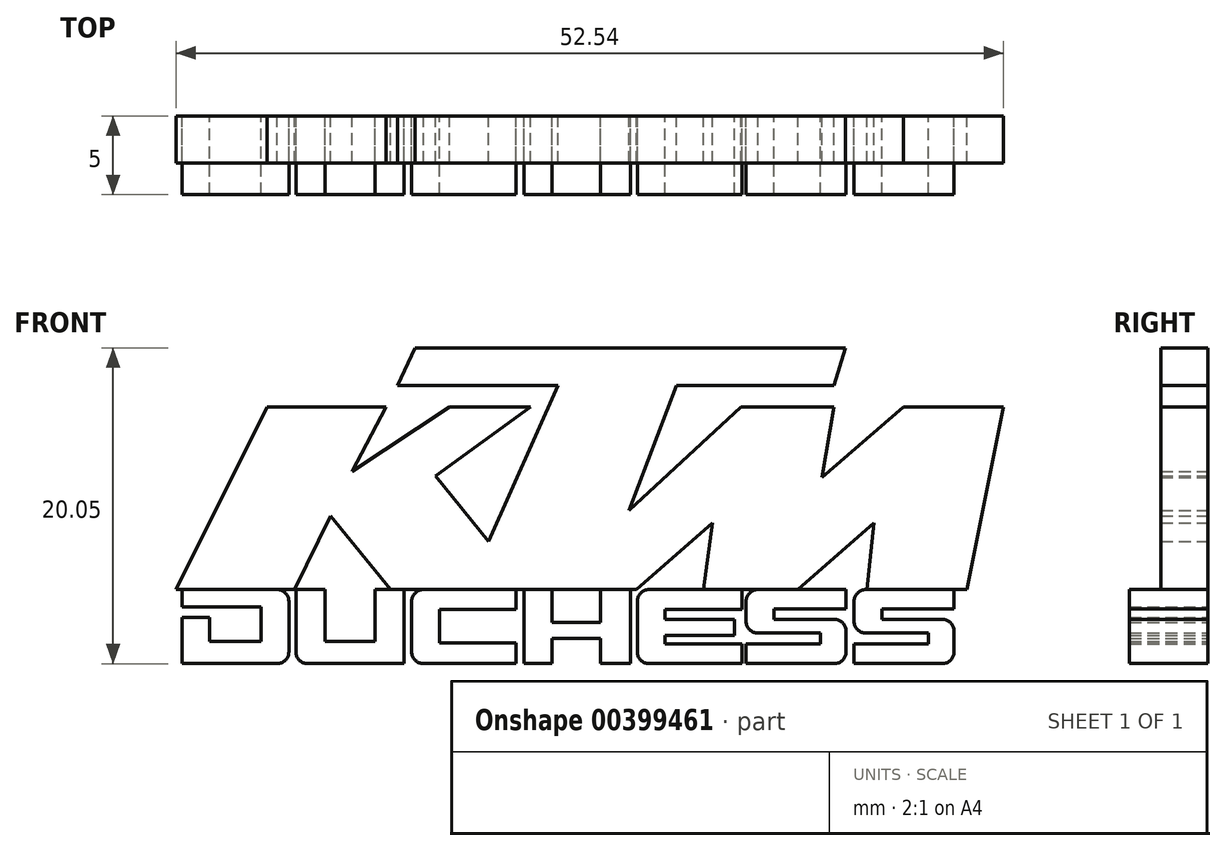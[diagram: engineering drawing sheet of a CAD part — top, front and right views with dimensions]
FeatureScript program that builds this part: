
annotation { "Feature Type Name" : "Feature", "Feature Type Description" : "" }
export const myFeature = defineFeature(function(context is Context, id is Id, definition is map)
    precondition{}
    {
        {
            var Q0;
            Q0=qCreatedBy(makeId("Front.planeOp"),FACE);
            var sketch = newSketch(context, id + "F0", { "sketchPlane" : qUnion([Q0])});
            skLineSegment(sketch, "E0", {"start": v(-21, 3.08) * mm, "end": v(-26.77, -8.53) * mm});
            skLineSegment(sketch, "E1", {"start": v(-19.24, -8.53) * mm, "end": v(-16.95, -3.85) * mm});
            skLineSegment(sketch, "E2", {"start": v(-16.95, -3.85) * mm, "end": v(-13.14, -8.53) * mm});
            skLineSegment(sketch, "E3", {"start": v(2.46, -8.53) * mm, "end": v(7.3, -4.3) * mm});
            skLineSegment(sketch, "E4", {"start": v(7.3, -4.3) * mm, "end": v(6.73, -8.53) * mm});
            skLineSegment(sketch, "E5", {"start": v(12.72, -8.53) * mm, "end": v(17.55, -4.3) * mm});
            skLineSegment(sketch, "E6", {"start": v(17.55, -4.3) * mm, "end": v(17.09, -8.53) * mm});
            skLineSegment(sketch, "E7", {"start": v(22.64, -8.53) * mm, "end": v(23.45, -8.53) * mm});
            skLineSegment(sketch, "E8", {"start": v(23.45, -8.53) * mm, "end": v(25.77, 3.08) * mm});
            skLineSegment(sketch, "E9", {"start": v(25.77, 3.08) * mm, "end": v(19.43, 3.08) * mm});
            skLineSegment(sketch, "E10", {"start": v(19.43, 3.08) * mm, "end": v(14.26, -1.4) * mm});
            skLineSegment(sketch, "E11", {"start": v(14.26, -1.4) * mm, "end": v(15.01, 3.08) * mm});
            skLineSegment(sketch, "E12", {"start": v(15.01, 3.08) * mm, "end": v(9.11, 3.08) * mm});
            skLineSegment(sketch, "E13", {"start": v(9.11, 3.08) * mm, "end": v(1.98, -3.5) * mm});
            skLineSegment(sketch, "E14", {"start": v(1.98, -3.5) * mm, "end": v(5, 4.43) * mm});
            skLineSegment(sketch, "E15", {"start": v(5, 4.43) * mm, "end": v(15.01, 4.43) * mm});
            skLineSegment(sketch, "E16", {"start": v(15.01, 4.43) * mm, "end": v(15.73, 6.81) * mm});
            skLineSegment(sketch, "E17", {"start": v(-11.58, 6.81) * mm, "end": v(-12.71, 4.43) * mm});
            skLineSegment(sketch, "E18", {"start": v(-12.71, 4.43) * mm, "end": v(-2.53, 4.43) * mm});
            skLineSegment(sketch, "E19", {"start": v(-2.53, 4.43) * mm, "end": v(-6.92, -5.47) * mm});
            skLineSegment(sketch, "E20", {"start": v(-6.92, -5.47) * mm, "end": v(-10.29, -1.32) * mm});
            skLineSegment(sketch, "E21", {"start": v(-10.29, -1.32) * mm, "end": v(-4.27, 3.08) * mm});
            skLineSegment(sketch, "E22", {"start": v(-4.27, 3.08) * mm, "end": v(-9.42, 3.08) * mm});
            skLineSegment(sketch, "E23", {"start": v(-9.42, 3.08) * mm, "end": v(-15.58, -1.03) * mm});
            skLineSegment(sketch, "E24", {"start": v(-15.58, -1.03) * mm, "end": v(-13.45, 3.08) * mm});
            skLineSegment(sketch, "E25", {"start": v(-13.45, 3.08) * mm, "end": v(-21, 3.08) * mm});
            skLineSegment(sketch, "E26", {"start": v(-26.4, -8.53) * mm, "end": v(-26.4, -9.64) * mm});
            skLineSegment(sketch, "E27", {"start": v(-26.4, -13.24) * mm, "end": v(-20.36, -13.24) * mm});
            skLineSegment(sketch, "E28", {"start": v(-19.6, -12.49) * mm, "end": v(-19.6, -9.28) * mm});
            skPoint(sketch, "E29.visualSharp", {"position": v(-19.6, -8.53) * mm});
            skArc(sketch, "E29.filletArc", {"start": v(-19.6, -9.28) * mm, "mid": v(-19.83, -8.75) * mm, "end": v(-20.36, -8.53) * mm});
            skPoint(sketch, "E30.visualSharp", {"position": v(-19.6, -13.24) * mm});
            skArc(sketch, "E30.filletArc", {"start": v(-20.36, -13.24) * mm, "mid": v(-19.83, -13.02) * mm, "end": v(-19.6, -12.49) * mm});
            skLineSegment(sketch, "E31", {"start": v(-24.66, -10.31) * mm, "end": v(-24.66, -11.84) * mm});
            skLineSegment(sketch, "E32", {"start": v(-24.66, -11.84) * mm, "end": v(-21.39, -11.84) * mm});
            skLineSegment(sketch, "E33", {"start": v(-21.39, -11.84) * mm, "end": v(-21.39, -9.64) * mm});
            skLineSegment(sketch, "E34", {"start": v(-21.39, -9.64) * mm, "end": v(-26.4, -9.64) * mm});
            skLineSegment(sketch, "E35", {"start": v(-24.66, -10.31) * mm, "end": v(-26.4, -10.31) * mm});
            skLineSegment(sketch, "E36.trimOffspring", {"start": v(-26.4, -10.31) * mm, "end": v(-26.4, -13.24) * mm});
            skLineSegment(sketch, "E37", {"start": v(-20.36, -8.53) * mm, "end": v(-19.17, -8.53) * mm, "construction": true});
            skLineSegment(sketch, "E38", {"start": v(-19.17, -8.53) * mm, "end": v(-19.17, -12.49) * mm});
            skLineSegment(sketch, "E39", {"start": v(-17.3, -8.53) * mm, "end": v(-17.3, -11.81) * mm});
            skLineSegment(sketch, "E40", {"start": v(-17.3, -11.81) * mm, "end": v(-14.13, -11.81) * mm});
            skLineSegment(sketch, "E41", {"start": v(-14.13, -11.81) * mm, "end": v(-14.13, -8.53) * mm});
            skLineSegment(sketch, "E42", {"start": v(-14.13, -8.53) * mm, "end": v(-13.14, -8.53) * mm});
            skLineSegment(sketch, "E43", {"start": v(-12.28, -8.53) * mm, "end": v(-12.28, -13.24) * mm});
            skLineSegment(sketch, "E44", {"start": v(-12.28, -13.24) * mm, "end": v(-18.42, -13.24) * mm});
            skPoint(sketch, "E45.visualSharp", {"position": v(-19.17, -13.24) * mm});
            skArc(sketch, "E45.filletArc", {"start": v(-19.17, -12.49) * mm, "mid": v(-18.95, -13.02) * mm, "end": v(-18.42, -13.24) * mm});
            skLineSegment(sketch, "E46", {"start": v(-19.17, -8.53) * mm, "end": v(-17.3, -8.53) * mm});
            skLineSegment(sketch, "E47", {"start": v(-11.82, -9.28) * mm, "end": v(-11.82, -12.49) * mm});
            skLineSegment(sketch, "E48", {"start": v(-5.18, -8.53) * mm, "end": v(-5.18, -9.8) * mm});
            skLineSegment(sketch, "E49", {"start": v(-5.18, -9.8) * mm, "end": v(-10.05, -9.8) * mm});
            skLineSegment(sketch, "E50", {"start": v(-10.05, -9.8) * mm, "end": v(-10.05, -11.91) * mm});
            skLineSegment(sketch, "E51", {"start": v(-10.05, -11.91) * mm, "end": v(-5.18, -11.91) * mm});
            skLineSegment(sketch, "E52", {"start": v(-5.18, -11.91) * mm, "end": v(-5.18, -13.24) * mm});
            skLineSegment(sketch, "E53", {"start": v(-11.07, -13.24) * mm, "end": v(-5.18, -13.24) * mm});
            skPoint(sketch, "E54.visualSharp", {"position": v(-11.82, -13.24) * mm});
            skArc(sketch, "E54.filletArc", {"start": v(-11.82, -12.49) * mm, "mid": v(-11.6, -13.02) * mm, "end": v(-11.07, -13.24) * mm});
            skPoint(sketch, "E55.visualSharp", {"position": v(-11.82, -8.53) * mm});
            skArc(sketch, "E55.filletArc", {"start": v(-11.07, -8.53) * mm, "mid": v(-11.6, -8.75) * mm, "end": v(-11.82, -9.28) * mm});
            skLineSegment(sketch, "E56", {"start": v(-4.69, -8.53) * mm, "end": v(-4.69, -13.24) * mm});
            skLineSegment(sketch, "E57", {"start": v(-4.69, -13.24) * mm, "end": v(-2.9, -13.24) * mm});
            skLineSegment(sketch, "E58", {"start": v(-2.9, -13.24) * mm, "end": v(-2.9, -11.62) * mm});
            skLineSegment(sketch, "E59", {"start": v(-2.9, -11.62) * mm, "end": v(0.17, -11.62) * mm});
            skLineSegment(sketch, "E60", {"start": v(0.17, -11.62) * mm, "end": v(0.17, -13.24) * mm});
            skLineSegment(sketch, "E61", {"start": v(0.17, -13.24) * mm, "end": v(2.1, -13.24) * mm});
            skLineSegment(sketch, "E62", {"start": v(2.1, -13.24) * mm, "end": v(2.1, -8.53) * mm});
            skLineSegment(sketch, "E63", {"start": v(0.17, -8.53) * mm, "end": v(0.17, -10.63) * mm});
            skLineSegment(sketch, "E64", {"start": v(0.17, -10.63) * mm, "end": v(-2.9, -10.63) * mm});
            skLineSegment(sketch, "E65", {"start": v(-2.9, -10.63) * mm, "end": v(-2.9, -8.53) * mm});
            skLineSegment(sketch, "E66", {"start": v(2.52, -9.28) * mm, "end": v(2.52, -12.49) * mm});
            skLineSegment(sketch, "E67", {"start": v(9.16, -8.53) * mm, "end": v(9.16, -9.8) * mm});
            skLineSegment(sketch, "E68", {"start": v(9.16, -9.8) * mm, "end": v(4.28, -9.8) * mm});
            skLineSegment(sketch, "E69", {"start": v(4.28, -9.8) * mm, "end": v(4.28, -10.41) * mm});
            skLineSegment(sketch, "E70", {"start": v(4.28, -12) * mm, "end": v(9.16, -12) * mm});
            skLineSegment(sketch, "E71", {"start": v(9.16, -12) * mm, "end": v(9.16, -13.24) * mm});
            skLineSegment(sketch, "E72", {"start": v(3.27, -13.24) * mm, "end": v(9.16, -13.24) * mm});
            skPoint(sketch, "E73.visualSharp", {"position": v(2.52, -13.24) * mm});
            skArc(sketch, "E73.filletArc", {"start": v(2.52, -12.49) * mm, "mid": v(2.74, -13.02) * mm, "end": v(3.27, -13.24) * mm});
            skLineSegment(sketch, "E74", {"start": v(3.27, -8.53) * mm, "end": v(6.73, -8.53) * mm});
            skPoint(sketch, "E75.visualSharp", {"position": v(2.52, -8.53) * mm});
            skArc(sketch, "E75.filletArc", {"start": v(3.27, -8.53) * mm, "mid": v(2.74, -8.75) * mm, "end": v(2.52, -9.28) * mm});
            skLineSegment(sketch, "E76", {"start": v(8.69, -10.41) * mm, "end": v(4.28, -10.41) * mm});
            skLineSegment(sketch, "E77", {"start": v(8.69, -10.41) * mm, "end": v(8.69, -11.45) * mm});
            skLineSegment(sketch, "E78", {"start": v(8.69, -11.45) * mm, "end": v(4.28, -11.45) * mm});
            skLineSegment(sketch, "E79.trimOffspring", {"start": v(4.28, -11.45) * mm, "end": v(4.28, -12) * mm});
            skLineSegment(sketch, "E80", {"start": v(15.78, -8.53) * mm, "end": v(15.78, -9.77) * mm});
            skLineSegment(sketch, "E81", {"start": v(15.78, -9.77) * mm, "end": v(11.21, -9.77) * mm});
            skLineSegment(sketch, "E82", {"start": v(11.21, -9.77) * mm, "end": v(11.21, -10.42) * mm});
            skLineSegment(sketch, "E83", {"start": v(11.21, -10.42) * mm, "end": v(15.03, -10.42) * mm});
            skLineSegment(sketch, "E84", {"start": v(15.78, -11.17) * mm, "end": v(15.78, -12.49) * mm});
            skLineSegment(sketch, "E85", {"start": v(15.03, -13.24) * mm, "end": v(9.43, -13.24) * mm});
            skLineSegment(sketch, "E86", {"start": v(9.43, -13.24) * mm, "end": v(9.43, -12) * mm});
            skLineSegment(sketch, "E87", {"start": v(9.43, -12) * mm, "end": v(14.16, -12) * mm});
            skLineSegment(sketch, "E88", {"start": v(14.16, -12) * mm, "end": v(14.16, -11.3) * mm});
            skLineSegment(sketch, "E89", {"start": v(14.16, -11.3) * mm, "end": v(10.18, -11.3) * mm});
            skLineSegment(sketch, "E90", {"start": v(9.43, -10.55) * mm, "end": v(9.43, -9.28) * mm});
            skLineSegment(sketch, "E91", {"start": v(12.72, -8.53) * mm, "end": v(15.78, -8.53) * mm});
            skPoint(sketch, "E92.visualSharp", {"position": v(9.43, -8.53) * mm});
            skArc(sketch, "E92.filletArc", {"start": v(10.18, -8.53) * mm, "mid": v(9.65, -8.75) * mm, "end": v(9.43, -9.28) * mm});
            skPoint(sketch, "E93.visualSharp", {"position": v(9.43, -11.3) * mm});
            skArc(sketch, "E93.filletArc", {"start": v(9.43, -10.55) * mm, "mid": v(9.65, -11.08) * mm, "end": v(10.18, -11.3) * mm});
            skPoint(sketch, "E94.visualSharp", {"position": v(15.78, -10.42) * mm});
            skArc(sketch, "E94.filletArc", {"start": v(15.78, -11.17) * mm, "mid": v(15.56, -10.64) * mm, "end": v(15.03, -10.42) * mm});
            skPoint(sketch, "E95.visualSharp", {"position": v(15.78, -13.24) * mm});
            skArc(sketch, "E95.filletArc", {"start": v(15.03, -13.24) * mm, "mid": v(15.56, -13.02) * mm, "end": v(15.78, -12.49) * mm});
            skLineSegment(sketch, "E96", {"start": v(22.64, -8.53) * mm, "end": v(22.64, -9.77) * mm});
            skLineSegment(sketch, "E97", {"start": v(22.64, -9.77) * mm, "end": v(18.07, -9.77) * mm});
            skLineSegment(sketch, "E98", {"start": v(18.07, -9.77) * mm, "end": v(18.07, -10.42) * mm});
            skLineSegment(sketch, "E99", {"start": v(18.07, -10.42) * mm, "end": v(21.89, -10.42) * mm});
            skLineSegment(sketch, "E100", {"start": v(22.64, -11.17) * mm, "end": v(22.64, -12.49) * mm});
            skLineSegment(sketch, "E101", {"start": v(21.89, -13.24) * mm, "end": v(16.29, -13.24) * mm});
            skLineSegment(sketch, "E102", {"start": v(16.29, -13.24) * mm, "end": v(16.29, -12) * mm});
            skLineSegment(sketch, "E103", {"start": v(16.29, -12) * mm, "end": v(21.02, -12) * mm});
            skLineSegment(sketch, "E104", {"start": v(21.02, -12) * mm, "end": v(21.02, -11.3) * mm});
            skLineSegment(sketch, "E105", {"start": v(21.02, -11.3) * mm, "end": v(17.04, -11.3) * mm});
            skLineSegment(sketch, "E106", {"start": v(16.29, -10.55) * mm, "end": v(16.29, -9.28) * mm});
            skLineSegment(sketch, "E107", {"start": v(17.04, -8.53) * mm, "end": v(17.09, -8.53) * mm});
            skPoint(sketch, "E108.visualSharp", {"position": v(16.29, -8.53) * mm});
            skArc(sketch, "E108.filletArc", {"start": v(17.04, -8.53) * mm, "mid": v(16.5, -8.75) * mm, "end": v(16.29, -9.28) * mm});
            skPoint(sketch, "E109.visualSharp", {"position": v(16.29, -11.3) * mm});
            skArc(sketch, "E109.filletArc", {"start": v(16.29, -10.55) * mm, "mid": v(16.5, -11.08) * mm, "end": v(17.04, -11.3) * mm});
            skPoint(sketch, "E110.visualSharp", {"position": v(22.64, -10.42) * mm});
            skArc(sketch, "E110.filletArc", {"start": v(22.64, -11.17) * mm, "mid": v(22.42, -10.64) * mm, "end": v(21.89, -10.42) * mm});
            skPoint(sketch, "E111.visualSharp", {"position": v(22.64, -13.24) * mm});
            skArc(sketch, "E111.filletArc", {"start": v(21.89, -13.24) * mm, "mid": v(22.42, -13.02) * mm, "end": v(22.64, -12.49) * mm});
            skLineSegment(sketch, "E112", {"start": v(23.45, -8.53) * mm, "end": v(22.64, -8.53) * mm});
            skPoint(sketch, "E113.orphan", {"position": v(-13.45, -8.15) * mm});
            skPoint(sketch, "E114.orphan", {"position": v(-19.05, -8.15) * mm});
            skLineSegment(sketch, "E115.trimOffspring", {"start": v(10.18, -8.53) * mm, "end": v(9.16, -8.53) * mm});
            skLineSegment(sketch, "E116.trimOffspring", {"start": v(2.46, -8.53) * mm, "end": v(2.1, -8.53) * mm});
            skLineSegment(sketch, "E117.trimOffspring", {"start": v(-19.24, -8.53) * mm, "end": v(-20.36, -8.53) * mm});
            skLineSegment(sketch, "E118.trimOffspring", {"start": v(-4.69, -8.53) * mm, "end": v(-5.18, -8.53) * mm});
            skLineSegment(sketch, "E119.trimOffspring", {"start": v(-11.07, -8.53) * mm, "end": v(-12.28, -8.53) * mm});
            skLineSegment(sketch, "E120.trimOffspring", {"start": v(-26.4, -8.53) * mm, "end": v(-26.77, -8.53) * mm});
            skLineSegment(sketch, "E121", {"start": v(-2.9, -8.53) * mm, "end": v(0.17, -8.53) * mm});
            skLineSegment(sketch, "E122", {"start": v(-11.58, 6.81) * mm, "end": v(15.73, 6.81) * mm});
            skSolve(sketch);
        }
        {
            var Q0;
            Q0 = qSketchRegion(id + "F0", true);
            extrude(context, id + "F1", {"entities" : qUnion([Q0]), "depth" : 5 * mm});
        }
        {
            var Q0;
            Q0=makeQuery(id+"F1.opExtrude","CAP_FACE",FACE,{"disambiguationData":[OSD([sQuery(id+"F0.wireOp",EDGE,"E0"),sQuery(id+"F0.wireOp",EDGE,"E1"),sQuery(id+"F0.wireOp",EDGE,"E2"),sQuery(id+"F0.wireOp",EDGE,"E3"),sQuery(id+"F0.wireOp",EDGE,"E4"),sQuery(id+"F0.wireOp",EDGE,"E5"),sQuery(id+"F0.wireOp",EDGE,"E6"),sQuery(id+"F0.wireOp",EDGE,"E8"),sQuery(id+"F0.wireOp",EDGE,"E9"),sQuery(id+"F0.wireOp",EDGE,"E10"),sQuery(id+"F0.wireOp",EDGE,"E11"),sQuery(id+"F0.wireOp",EDGE,"E12"),sQuery(id+"F0.wireOp",EDGE,"E13"),sQuery(id+"F0.wireOp",EDGE,"E14"),sQuery(id+"F0.wireOp",EDGE,"E15"),sQuery(id+"F0.wireOp",EDGE,"E16"),sQuery(id+"F0.wireOp",EDGE,"3NEIWcZY-8mkg-9U7g-S424-nP58Ebou9Cct"),sQuery(id+"F0.wireOp",EDGE,"E17"),sQuery(id+"F0.wireOp",EDGE,"E18"),sQuery(id+"F0.wireOp",EDGE,"E19"),sQuery(id+"F0.wireOp",EDGE,"E20"),sQuery(id+"F0.wireOp",EDGE,"E21"),sQuery(id+"F0.wireOp",EDGE,"E22"),sQuery(id+"F0.wireOp",EDGE,"E23"),sQuery(id+"F0.wireOp",EDGE,"E24"),sQuery(id+"F0.wireOp",EDGE,"E25"),sQuery(id+"F0.wireOp",EDGE,"E26"),sQuery(id+"F0.wireOp",EDGE,"E27"),sQuery(id+"F0.wireOp",EDGE,"E28"),sQuery(id+"F0.wireOp",EDGE,"E29.filletArc"),sQuery(id+"F0.wireOp",EDGE,"E30.filletArc"),sQuery(id+"F0.wireOp",EDGE,"E31"),sQuery(id+"F0.wireOp",EDGE,"E32"),sQuery(id+"F0.wireOp",EDGE,"E33"),sQuery(id+"F0.wireOp",EDGE,"E34"),sQuery(id+"F0.wireOp",EDGE,"E35"),sQuery(id+"F0.wireOp",EDGE,"E36.trimOffspring"),sQuery(id+"F0.wireOp",EDGE,"E38"),sQuery(id+"F0.wireOp",EDGE,"E39"),sQuery(id+"F0.wireOp",EDGE,"E40"),sQuery(id+"F0.wireOp",EDGE,"E41"),sQuery(id+"F0.wireOp",EDGE,"E42"),sQuery(id+"F0.wireOp",EDGE,"E43"),sQuery(id+"F0.wireOp",EDGE,"E44"),sQuery(id+"F0.wireOp",EDGE,"E45.filletArc"),sQuery(id+"F0.wireOp",EDGE,"E46"),sQuery(id+"F0.wireOp",EDGE,"E47"),sQuery(id+"F0.wireOp",EDGE,"E48"),sQuery(id+"F0.wireOp",EDGE,"E49"),sQuery(id+"F0.wireOp",EDGE,"E50"),sQuery(id+"F0.wireOp",EDGE,"E51"),sQuery(id+"F0.wireOp",EDGE,"E52"),sQuery(id+"F0.wireOp",EDGE,"E53"),sQuery(id+"F0.wireOp",EDGE,"E54.filletArc"),sQuery(id+"F0.wireOp",EDGE,"E55.filletArc"),sQuery(id+"F0.wireOp",EDGE,"E56"),sQuery(id+"F0.wireOp",EDGE,"E57"),sQuery(id+"F0.wireOp",EDGE,"E58"),sQuery(id+"F0.wireOp",EDGE,"E59"),sQuery(id+"F0.wireOp",EDGE,"E60"),sQuery(id+"F0.wireOp",EDGE,"E61"),sQuery(id+"F0.wireOp",EDGE,"E62"),sQuery(id+"F0.wireOp",EDGE,"E63"),sQuery(id+"F0.wireOp",EDGE,"E64"),sQuery(id+"F0.wireOp",EDGE,"E65"),sQuery(id+"F0.wireOp",EDGE,"E66"),sQuery(id+"F0.wireOp",EDGE,"E67"),sQuery(id+"F0.wireOp",EDGE,"E68"),sQuery(id+"F0.wireOp",EDGE,"E69"),sQuery(id+"F0.wireOp",EDGE,"E70"),sQuery(id+"F0.wireOp",EDGE,"E71"),sQuery(id+"F0.wireOp",EDGE,"E72"),sQuery(id+"F0.wireOp",EDGE,"E73.filletArc"),sQuery(id+"F0.wireOp",EDGE,"E74"),sQuery(id+"F0.wireOp",EDGE,"E75.filletArc"),sQuery(id+"F0.wireOp",EDGE,"E76"),sQuery(id+"F0.wireOp",EDGE,"E77"),sQuery(id+"F0.wireOp",EDGE,"E78"),sQuery(id+"F0.wireOp",EDGE,"E79.trimOffspring"),sQuery(id+"F0.wireOp",EDGE,"E80"),sQuery(id+"F0.wireOp",EDGE,"E81"),sQuery(id+"F0.wireOp",EDGE,"E82"),sQuery(id+"F0.wireOp",EDGE,"E83"),sQuery(id+"F0.wireOp",EDGE,"E84"),sQuery(id+"F0.wireOp",EDGE,"E85"),sQuery(id+"F0.wireOp",EDGE,"E86"),sQuery(id+"F0.wireOp",EDGE,"E87"),sQuery(id+"F0.wireOp",EDGE,"E88"),sQuery(id+"F0.wireOp",EDGE,"E89"),sQuery(id+"F0.wireOp",EDGE,"E90"),sQuery(id+"F0.wireOp",EDGE,"E91"),sQuery(id+"F0.wireOp",EDGE,"E92.filletArc"),sQuery(id+"F0.wireOp",EDGE,"E93.filletArc"),sQuery(id+"F0.wireOp",EDGE,"E94.filletArc"),sQuery(id+"F0.wireOp",EDGE,"E95.filletArc"),sQuery(id+"F0.wireOp",EDGE,"E96"),sQuery(id+"F0.wireOp",EDGE,"E97"),sQuery(id+"F0.wireOp",EDGE,"E98"),sQuery(id+"F0.wireOp",EDGE,"E99"),sQuery(id+"F0.wireOp",EDGE,"E100"),sQuery(id+"F0.wireOp",EDGE,"E101"),sQuery(id+"F0.wireOp",EDGE,"E102"),sQuery(id+"F0.wireOp",EDGE,"E103"),sQuery(id+"F0.wireOp",EDGE,"E104"),sQuery(id+"F0.wireOp",EDGE,"E105"),sQuery(id+"F0.wireOp",EDGE,"E106"),sQuery(id+"F0.wireOp",EDGE,"E107"),sQuery(id+"F0.wireOp",EDGE,"E108.filletArc"),sQuery(id+"F0.wireOp",EDGE,"E109.filletArc"),sQuery(id+"F0.wireOp",EDGE,"E110.filletArc"),sQuery(id+"F0.wireOp",EDGE,"E111.filletArc"),sQuery(id+"F0.wireOp",EDGE,"E112"),sQuery(id+"F0.wireOp",EDGE,"E115.trimOffspring"),sQuery(id+"F0.wireOp",EDGE,"E116.trimOffspring"),sQuery(id+"F0.wireOp",EDGE,"E117.trimOffspring"),sQuery(id+"F0.wireOp",EDGE,"E118.trimOffspring"),sQuery(id+"F0.wireOp",EDGE,"E119.trimOffspring"),sQuery(id+"F0.wireOp",EDGE,"E120.trimOffspring"),sQuery(id+"F0.wireOp",EDGE,"E121")])],"isStart":false});
            var sketch = newSketch(context, id + "F2", { "sketchPlane" : qUnion([Q0])});
            skLineSegment(sketch, "E123.bottom", {"start": v(-26.77, -8.53) * mm, "end": v(26.52, -8.53) * mm});
            skLineSegment(sketch, "E123.top", {"start": v(-26.77, 7.13) * mm, "end": v(26.52, 7.13) * mm});
            skLineSegment(sketch, "E123.left", {"start": v(-26.77, -8.53) * mm, "end": v(-26.77, 7.13) * mm});
            skLineSegment(sketch, "E123.right", {"start": v(26.52, -8.53) * mm, "end": v(26.52, 7.13) * mm});
            skSolve(sketch);
        }
        {
            var Q0;
            Q0 = qSketchRegion(id + "F2", true);
            extrude(context, id + "F3", {"entities" : qUnion([Q0]), "operationType" : NewBodyOperationType.REMOVE, "oppositeDirection" : true, "depth" : 2 * mm});
        }
    });
